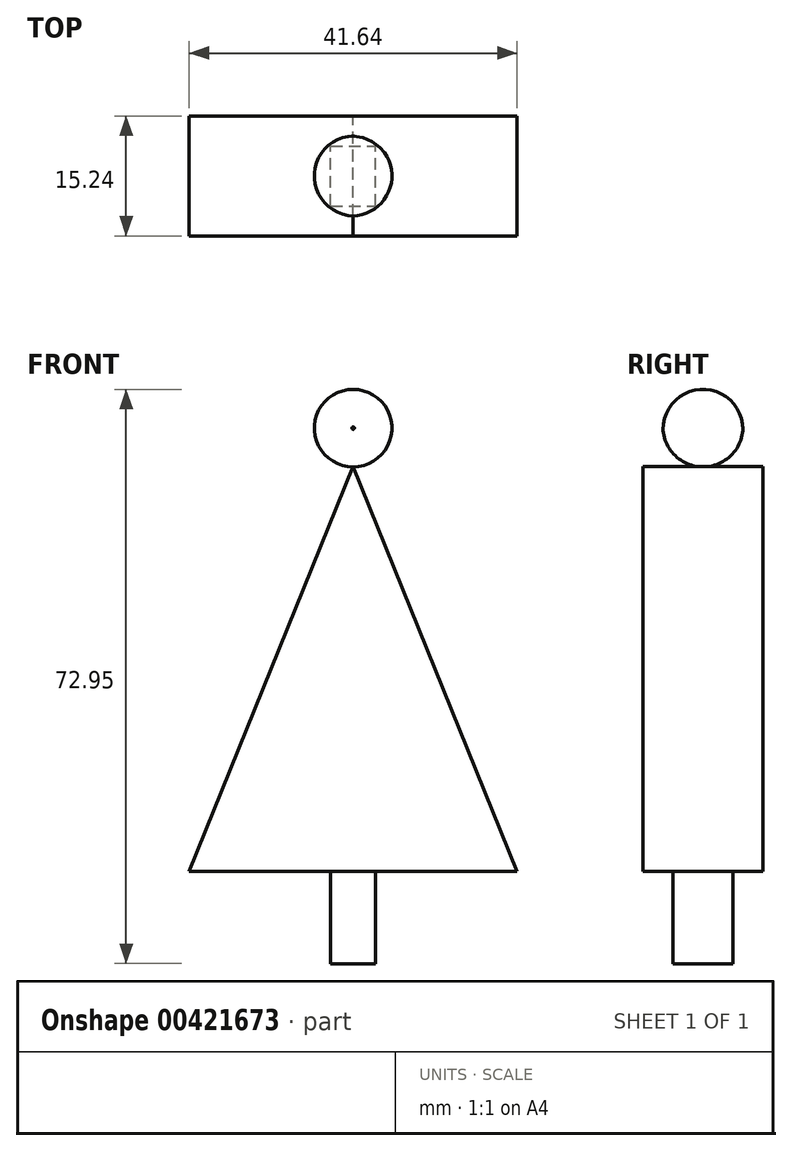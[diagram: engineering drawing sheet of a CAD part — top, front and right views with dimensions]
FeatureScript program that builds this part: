
annotation { "Feature Type Name" : "Feature", "Feature Type Description" : "" }
export const myFeature = defineFeature(function(context is Context, id is Id, definition is map)
    precondition{}
    {
        {
            var Q0;
            Q0=qCreatedBy(makeId("Front.planeOp"),FACE);
            var sketch = newSketch(context, id + "F0", { "sketchPlane" : qUnion([Q0])});
            skCircle(sketch, "E0", {"center": v(0, 56.34) * mm, "radius": 5.24 * mm});
            skSolve(sketch);
        }
        {
            var Q0;
            Q0=qCreatedBy(makeId("Front.planeOp"),FACE);
            var sketch = newSketch(context, id + "F1", { "sketchPlane" : qUnion([Q0])});
            skLineSegment(sketch, "E1", {"start": v(0, 51.49) * mm, "end": v(-20.82, 0) * mm});
            skLineSegment(sketch, "E2", {"start": v(0, 51.49) * mm, "end": v(20.82, 0) * mm});
            skLineSegment(sketch, "E3", {"start": v(20.82, 0) * mm, "end": v(-20.82, 0) * mm});
            skSolve(sketch);
        }
        {
            var Q0;
            Q0=qCreatedBy(makeId("Front.planeOp"),FACE);
            var sketch = newSketch(context, id + "F2", { "sketchPlane" : qUnion([Q0])});
            skLineSegment(sketch, "E4.bottom", {"start": v(-2.85, 0) * mm, "end": v(2.85, 0) * mm});
            skLineSegment(sketch, "E4.top", {"start": v(-2.85, -11.7) * mm, "end": v(2.85, -11.7) * mm});
            skLineSegment(sketch, "E4.left", {"start": v(-2.85, 0) * mm, "end": v(-2.85, -11.7) * mm});
            skLineSegment(sketch, "E4.right", {"start": v(2.85, 0) * mm, "end": v(2.85, -11.7) * mm});
            skPoint(sketch, "E4.middle", {"position": v(0, -5.85) * mm});
            skSolve(sketch);
        }
        {
            var Q0;
            Q0=makeQuery(id+"F0.imprint","IMPRINT",FACE,{"disambiguationData":[TD([[makeQuery(id+"F0.imprint","IMPRINT",EDGE,{"derivedFrom":sQuery(id+"F0.wireOp",EDGE,"E0")}),1.0]])]});
            extrude(context, id + "F3", {"entities" : qUnion([Q0]), "depth" : 5.08 * mm});
        }
        {
            var Q0;
            Q0=makeQuery(id+"F3.opExtrude","CAP_EDGE",EDGE,{"disambiguationData":[OSD([sQuery(id+"F0.wireOp",EDGE,"E0")])],"isStart":false});
            fillet(context, id + "F4", {"entities" : qUnion([Q0]), "radius" : 5.08 * mm, "tangentPropagation" : true, "allowEdgeOverflow" : false});
        }
        {
            var Q0;
            Q0=makeQuery(id+"F3.opExtrude","SWEPT_BODY",BODY,{"disambiguationData":[OSD([sQuery(id+"F0.wireOp",EDGE,"E0")])]});
            var Q1;
            Q1=qCreatedBy(makeId("Front.planeOp"),FACE);
            mirror(context, id + "F5", {"operationType" : NewBodyOperationType.ADD, "entities" : qUnion([Q0]), "mirrorPlane" : qUnion([Q1])});
        }
        {
            var Q0;
            Q0 = qSketchRegion(id + "F2", true);
            extrude(context, id + "F6", {"entities" : qUnion([Q0]), "operationType" : NewBodyOperationType.ADD, "endBound" : BoundingType.SYMMETRIC, "depth" : 7.62 * mm});
        }
        {
            var Q0;
            Q0=makeQuery(id+"F1.imprint","IMPRINT",FACE,{"disambiguationData":[TD([[makeQuery(id+"F1.imprint","IMPRINT",EDGE,{"derivedFrom":sQuery(id+"F1.wireOp",EDGE,"E1")}),1.0]])]});
            extrude(context, id + "F7", {"entities" : qUnion([Q0]), "endBound" : BoundingType.SYMMETRIC, "depth" : 15.24 * mm});
        }
    });
